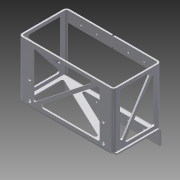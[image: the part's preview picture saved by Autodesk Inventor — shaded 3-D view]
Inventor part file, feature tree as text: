
AUTODESK INVENTOR PART (.ipt)
format: ipt  version: 2015 SP1 (Build 190203100, 203)  size: 448,512 bytes
history: native  units: in
note: dims shown in document units (in); Inventor stores cm internally (conversion verified against a paired STEP export)
features: other x29, sheet_metal_op x12, sketch x6, projected_geometry x5, hole x3
ambient origin geometry x8: Origin, YZ Plane, XZ Plane, XY Plane, X Axis, Y Axis, Z Axis, Center Point
bodies: Solid1 (feature_tree)
feature tree (55):
  other  "<userpath>\Documents\2015 Offseason Chassis\West Coast Chassis Fall 2015\rivet(rv).xlsx"
  other  "front"
  other  "back_supporting"
  other  "back_mounting"
  other  "left_side"
  other  "right_side"
  other  "right_back"
  other  "left_back"
  hole  "bottom_rivet_holes"  [1 undecoded]
  other  "top_rivet_sketch"
  hole  "compressor_mounting_holes"  [1 undecoded]
  hole  "top_rivet_holes"  [1 undecoded]
  other  "front_sketch"
  other  "Plate1"
  sketch  "Sketch2"  dims[d0=7.1in d1=4.376in]
  other  "Plate2"
  sheet_metal_op  "Bend1"
  sheet_metal_op  "Corner1"
  sketch  "Sketch3"  dims[d2=0.12in d3=0.12in]
  other  "Plate3"
  sheet_metal_op  "Bend2"
  sheet_metal_op  "Corner2"
  sketch  "Sketch4"  dims[d4=0.06in d5=0.24in]
  other  "Plate4"
  sheet_metal_op  "Bend3"
  sheet_metal_op  "Corner3"
  sketch  "Sketch5"  dims[d6=0.12in]
  other  "Plate5"
  sheet_metal_op  "Bend4"
  sheet_metal_op  "Corner4"
  sketch  "Sketch8"  dims[d7=3.45in]
  other  "Plate8"
  sheet_metal_op  "Bend7"
  sheet_metal_op  "Corner7"
  sketch  "Sketch9"  dims[d8=90.0deg d9=0.12in d10=0.48in d11=0.12in d12=0.12in d13=0.12in d14=0.06in d15=0.24in d16=0.12in d17=1.0in d18=90.0deg d19=0.12in d20=0.48in d21=0.12in d22=0.12in d23=0.12in d24=0.06in d25=0.24in d26=0.12in d27=3.45in d28=90.0deg d29=0.12in d30=0.48in d31=0.12in d32=0.12in d33=0.12in d34=0.06in d35=0.24in d36=0.12in d37=3.45in d38=90.0deg d39=0.12in d40=0.48in d41=0.12in d42=0.12in d63=0.12in d64=0.06in d65=0.24in d66=0.12in d67=3.49in d68=90.0deg d69=0.12in d70=0.48in d71=0.12in d72=0.12in d73=0.12in d74=0.06in d75=0.24in d76=0.12in d77=3.49in d78=90.0deg d79=0.12in d80=0.48in d81=0.12in d82=0.12in d83=0.1406in d84=0.75in d85=0.375in d86=0.25in d87=0.5635in d88=0.12in d89=0.8108in d105=0.25in d106=1.42in d108=5.51in d109=0.25in d110=0.75in d111=0.375in d112=0.25in d113=0.5635in d114=0.12in d115=0.8108in d116=0.5in d117=0.1406in d118=0.75in d119=0.375in d120=0.25in d121=0.5635in d122=0.12in d123=0.8108in d124=0.25in d125=0.25in d126=0.25in d127=0.25in d128=0.25in d129=0.25in d130=0.25in d131=0.125in d132=0.12in d133=0.0in d134=0.25in d135=0.12in d136=0.0in d137=0.25in d138=0.25in d139=0.25in d140=0.25in d141=0.25in d142=0.25in d143=0.25in d144=0.125in d145=0.12in d146=0.0in d147=0.25in d148=0.25in d149=0.25in d150=0.25in d151=0.25in d152=0.25in d153=0.25in d154=0.125in d155=0.12in d156=0.0in d157=0.5in d158=0.25in d159=0.25in d160=0.25in d161=0.25in d162=0.25in d163=0.125in d164=0.12in d165=0.0in d166=0.5in]
  other  "Plate9"
  sheet_metal_op  "Bend8"
  sheet_metal_op  "Corner8"
  other  "bottom_rivet_sketch"
  projected_geometry  "Projected Loop1"
  other  "cmp_mountings_sketch"
  projected_geometry  "Projected Loop4"
  other  "front_speed_sketch"
  other  "back_speed_hole_sketch"
  other  "left_speed_sketch"
  projected_geometry  "Projected Loop5"
  other  "right_speed_sketch"
  projected_geometry  "Projected Loop6"
  other  "bottom_speed_sketch"
  projected_geometry  "Projected Loop7"
  other  "front_speed_cut"
  other  "back_speed_cut"
  other  "left_speed_cut"
  other  "right_speed_cut"
  other  "bottom_speed_cut"
note: 3 required parameter values undecoded (feature->parameter linkage not recoverable at this tier; creation-order binding heuristic only, values carry confidence <= 0.55)
